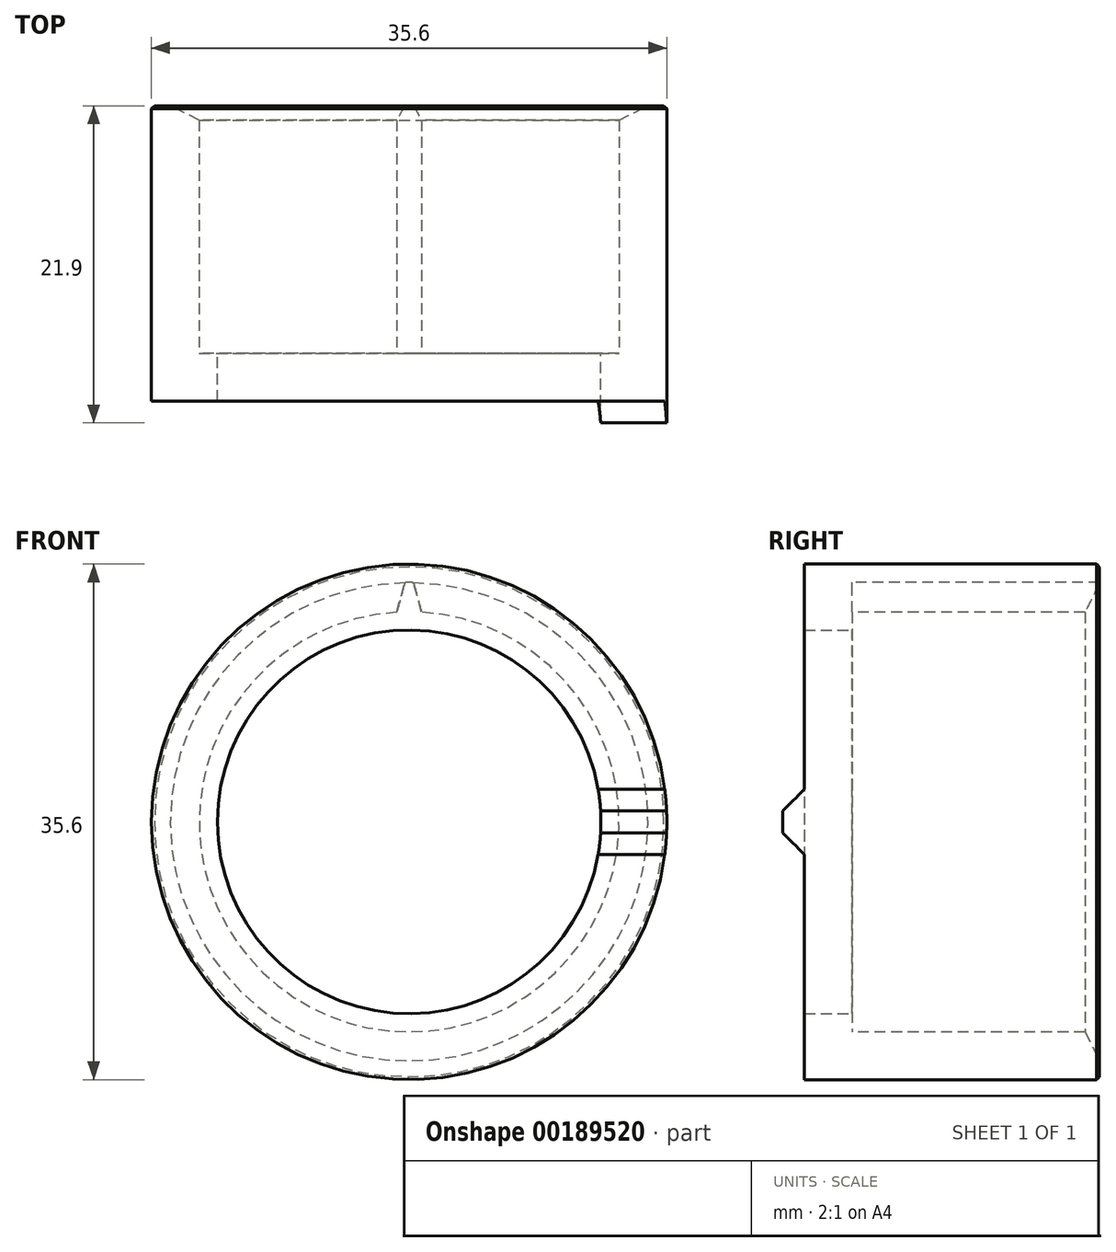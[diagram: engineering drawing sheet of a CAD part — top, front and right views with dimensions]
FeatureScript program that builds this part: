
annotation { "Feature Type Name" : "Feature", "Feature Type Description" : "" }
export const myFeature = defineFeature(function(context is Context, id is Id, definition is map)
    precondition{}
    {
        {
            var Q0;
            Q0=qCreatedBy(makeId("Front.planeOp"),FACE);
            var sketch = newSketch(context, id + "F0", { "sketchPlane" : qUnion([Q0])});
            skCircle(sketch, "E0", {"center": v(0, 0) * mm, "radius": 17.8 * mm});
            skCircle(sketch, "E1", {"center": v(0, 0) * mm, "radius": 14.5 * mm});
            skCircle(sketch, "E2", {"center": v(0, 0) * mm, "radius": 13.25 * mm});
            skSolve(sketch);
        }
        {
            var Q0;
            Q0=makeQuery(id+"F0.imprint","IMPRINT",FACE,{"disambiguationData":[TD([[makeQuery(id+"F0.imprint","IMPRINT",EDGE,{"derivedFrom":sQuery(id+"F0.wireOp",EDGE,"E0")}),1.0]])]});
            var Q1;
            Q1=makeQuery(id+"F0.imprint","IMPRINT",FACE,{"disambiguationData":[TD([[makeQuery(id+"F0.imprint","IMPRINT",EDGE,{"derivedFrom":sQuery(id+"F0.wireOp",EDGE,"E1")}),1.0]])]});
            extrude(context, id + "F1", {"entities" : qUnion([Q0, Q1]), "depth" : 3.3 * mm});
        }
        {
            var Q0;
            Q0=makeQuery(id+"F0.imprint","IMPRINT",FACE,{"disambiguationData":[TD([[makeQuery(id+"F0.imprint","IMPRINT",EDGE,{"derivedFrom":sQuery(id+"F0.wireOp",EDGE,"E0")}),1.0]])]});
            extrude(context, id + "F2", {"entities" : qUnion([Q0]), "operationType" : NewBodyOperationType.ADD, "oppositeDirection" : true, "depth" : (20.4 - 3.3) * mm});
        }
        {
            var Q0;
            Q0=makeQuery(id+"F2.opExtrude","CAP_EDGE",EDGE,{"disambiguationData":[OSD([sQuery(id+"F0.wireOp",EDGE,"E1")])],"isStart":false});
            chamfer(context, id + "F3", {"entities" : qUnion([Q0]), "chamferType" : ChamferType.TWO_OFFSETS, "width1" : 2 * mm, "oppositeDirection" : false, "width2" : 1 * mm, "tangentPropagation" : true});
        }
        {
            var Q0;
            Q0=qCreatedBy(makeId("Front.planeOp"),FACE);
            var sketch = newSketch(context, id + "F4", { "sketchPlane" : qUnion([Q0])});
            skLineSegment(sketch, "E3", {"start": v(0.38, -14.5) * mm, "end": v(1.1, -16.51) * mm});
            skArc(sketch, "E4", {"start": v(2.08, -14.35) * mm, "mid": v(2.45, -14.3) * mm, "end": v(2.82, -14.22) * mm});
            skArc(sketch, "E5", {"start": v(3.88, -16.09) * mm, "mid": v(4.17, -16.02) * mm, "end": v(4.46, -15.94) * mm});
            skLineSegment(sketch, "E6", {"start": v(-0.37, -14.5) * mm, "end": v(-1.1, -16.51) * mm});
            skLineSegment(sketch, "E7.1.0", {"start": v(2.82, -14.22) * mm, "end": v(3.88, -16.09) * mm});
            skLineSegment(sketch, "E7.1.1", {"start": v(2.08, -14.35) * mm, "end": v(1.7, -16.46) * mm});
            skLineSegment(sketch, "E7.2.0", {"start": v(5.18, -13.54) * mm, "end": v(6.55, -15.2) * mm});
            skLineSegment(sketch, "E7.2.1", {"start": v(4.48, -13.8) * mm, "end": v(4.46, -15.94) * mm});
            skLineSegment(sketch, "E7.3.0", {"start": v(7.4, -12.47) * mm, "end": v(9.02, -13.87) * mm});
            skLineSegment(sketch, "E7.3.1", {"start": v(6.74, -12.84) * mm, "end": v(7.08, -14.96) * mm});
            skLineSegment(sketch, "E7.4.0", {"start": v(9.4, -11.04) * mm, "end": v(11.24, -12.15) * mm});
            skLineSegment(sketch, "E7.4.1", {"start": v(8.81, -11.51) * mm, "end": v(9.51, -13.54) * mm});
            skLineSegment(sketch, "E7.5.0", {"start": v(11.13, -9.3) * mm, "end": v(13.13, -10.08) * mm});
            skLineSegment(sketch, "E7.5.1", {"start": v(10.63, -9.86) * mm, "end": v(11.66, -11.74) * mm});
            skLineSegment(sketch, "E7.6.0", {"start": v(12.54, -7.28) * mm, "end": v(14.64, -7.71) * mm});
            skLineSegment(sketch, "E7.6.1", {"start": v(12.15, -7.92) * mm, "end": v(13.48, -9.6) * mm});
            skLineSegment(sketch, "E7.7.0", {"start": v(13.59, -5.06) * mm, "end": v(15.74, -5.13) * mm});
            skLineSegment(sketch, "E7.7.1", {"start": v(13.31, -5.75) * mm, "end": v(14.9, -7.19) * mm});
            skLineSegment(sketch, "E7.8.0", {"start": v(14.25, -2.69) * mm, "end": v(16.38, -2.4) * mm});
            skLineSegment(sketch, "E7.8.1", {"start": v(14.1, -3.42) * mm, "end": v(15.9, -4.56) * mm});
            skLineSegment(sketch, "E7.9.0", {"start": v(14.5, -0.24) * mm, "end": v(16.54, 0.4) * mm});
            skLineSegment(sketch, "E7.9.1", {"start": v(14.47, -0.99) * mm, "end": v(16.45, -1.8) * mm});
            skLineSegment(sketch, "E7.10.0", {"start": v(14.33, 2.21) * mm, "end": v(16.24, 3.2) * mm});
            skLineSegment(sketch, "E7.10.1", {"start": v(14.43, 1.47) * mm, "end": v(16.52, 1) * mm});
            skLineSegment(sketch, "E7.11.0", {"start": v(13.75, 4.6) * mm, "end": v(15.46, 5.9) * mm});
            skLineSegment(sketch, "E7.11.1", {"start": v(13.97, 3.89) * mm, "end": v(16.11, 3.77) * mm});
            skLineSegment(sketch, "E7.12.0", {"start": v(12.77, 6.86) * mm, "end": v(14.25, 8.42) * mm});
            skLineSegment(sketch, "E7.12.1", {"start": v(13.11, 6.2) * mm, "end": v(15.24, 6.44) * mm});
            skLineSegment(sketch, "E7.13.0", {"start": v(11.43, 8.92) * mm, "end": v(12.62, 10.71) * mm});
            skLineSegment(sketch, "E7.13.1", {"start": v(11.88, 8.32) * mm, "end": v(13.94, 8.93) * mm});
            skLineSegment(sketch, "E7.14.0", {"start": v(9.76, 10.72) * mm, "end": v(10.62, 12.69) * mm});
            skLineSegment(sketch, "E7.14.1", {"start": v(10.3, 10.2) * mm, "end": v(12.23, 11.15) * mm});
            skLineSegment(sketch, "E7.15.0", {"start": v(7.8, 12.22) * mm, "end": v(8.33, 14.3) * mm});
            skLineSegment(sketch, "E7.15.1", {"start": v(8.43, 11.8) * mm, "end": v(10.17, 13.06) * mm});
            skLineSegment(sketch, "E7.16.0", {"start": v(5.63, 13.36) * mm, "end": v(5.8, 15.5) * mm});
            skLineSegment(sketch, "E7.16.1", {"start": v(6.31, 13.05) * mm, "end": v(7.81, 14.59) * mm});
            skLineSegment(sketch, "E7.17.0", {"start": v(3.29, 14.12) * mm, "end": v(3.09, 16.26) * mm});
            skLineSegment(sketch, "E7.17.1", {"start": v(4.02, 13.93) * mm, "end": v(5.23, 15.7) * mm});
            skLineSegment(sketch, "E7.18.0", {"start": v(0.86, 14.47) * mm, "end": v(0.3, 16.55) * mm});
            skLineSegment(sketch, "E7.18.1", {"start": v(1.6, 14.41) * mm, "end": v(2.5, 16.36) * mm});
            skLineSegment(sketch, "E7.19.0", {"start": v(-1.6, 14.41) * mm, "end": v(-2.5, 16.36) * mm});
            skLineSegment(sketch, "E7.19.1", {"start": v(-0.86, 14.47) * mm, "end": v(-0.3, 16.55) * mm});
            skLineSegment(sketch, "E7.20.0", {"start": v(-4.02, 13.93) * mm, "end": v(-5.23, 15.7) * mm});
            skLineSegment(sketch, "E7.20.1", {"start": v(-3.29, 14.12) * mm, "end": v(-3.09, 16.26) * mm});
            skLineSegment(sketch, "E7.21.0", {"start": v(-6.31, 13.05) * mm, "end": v(-7.81, 14.59) * mm});
            skLineSegment(sketch, "E7.21.1", {"start": v(-5.63, 13.36) * mm, "end": v(-5.8, 15.5) * mm});
            skLineSegment(sketch, "E7.22.0", {"start": v(-8.43, 11.8) * mm, "end": v(-10.17, 13.06) * mm});
            skLineSegment(sketch, "E7.22.1", {"start": v(-7.8, 12.22) * mm, "end": v(-8.33, 14.3) * mm});
            skLineSegment(sketch, "E7.23.0", {"start": v(-10.3, 10.2) * mm, "end": v(-12.23, 11.15) * mm});
            skLineSegment(sketch, "E7.23.1", {"start": v(-9.76, 10.72) * mm, "end": v(-10.62, 12.69) * mm});
            skLineSegment(sketch, "E7.24.0", {"start": v(-11.88, 8.32) * mm, "end": v(-13.94, 8.93) * mm});
            skLineSegment(sketch, "E7.24.1", {"start": v(-11.43, 8.92) * mm, "end": v(-12.62, 10.71) * mm});
            skLineSegment(sketch, "E7.25.0", {"start": v(-13.11, 6.2) * mm, "end": v(-15.24, 6.44) * mm});
            skLineSegment(sketch, "E7.25.1", {"start": v(-12.77, 6.86) * mm, "end": v(-14.25, 8.42) * mm});
            skLineSegment(sketch, "E7.26.0", {"start": v(-13.97, 3.89) * mm, "end": v(-16.11, 3.77) * mm});
            skLineSegment(sketch, "E7.26.1", {"start": v(-13.75, 4.6) * mm, "end": v(-15.46, 5.9) * mm});
            skLineSegment(sketch, "E7.27.0", {"start": v(-14.43, 1.47) * mm, "end": v(-16.52, 1) * mm});
            skLineSegment(sketch, "E7.27.1", {"start": v(-14.33, 2.21) * mm, "end": v(-16.24, 3.2) * mm});
            skLineSegment(sketch, "E7.28.0", {"start": v(-14.47, -0.99) * mm, "end": v(-16.45, -1.8) * mm});
            skLineSegment(sketch, "E7.28.1", {"start": v(-14.5, -0.24) * mm, "end": v(-16.54, 0.4) * mm});
            skLineSegment(sketch, "E7.29.0", {"start": v(-14.1, -3.42) * mm, "end": v(-15.9, -4.56) * mm});
            skLineSegment(sketch, "E7.29.1", {"start": v(-14.25, -2.69) * mm, "end": v(-16.38, -2.4) * mm});
            skLineSegment(sketch, "E7.30.0", {"start": v(-13.31, -5.75) * mm, "end": v(-14.9, -7.19) * mm});
            skLineSegment(sketch, "E7.30.1", {"start": v(-13.59, -5.06) * mm, "end": v(-15.74, -5.13) * mm});
            skLineSegment(sketch, "E7.31.0", {"start": v(-12.15, -7.92) * mm, "end": v(-13.48, -9.6) * mm});
            skLineSegment(sketch, "E7.31.1", {"start": v(-12.54, -7.28) * mm, "end": v(-14.64, -7.71) * mm});
            skLineSegment(sketch, "E7.32.0", {"start": v(-10.63, -9.86) * mm, "end": v(-11.66, -11.74) * mm});
            skLineSegment(sketch, "E7.32.1", {"start": v(-11.13, -9.3) * mm, "end": v(-13.13, -10.08) * mm});
            skLineSegment(sketch, "E7.33.0", {"start": v(-8.81, -11.51) * mm, "end": v(-9.51, -13.54) * mm});
            skLineSegment(sketch, "E7.33.1", {"start": v(-9.4, -11.04) * mm, "end": v(-11.24, -12.15) * mm});
            skLineSegment(sketch, "E7.34.0", {"start": v(-6.74, -12.84) * mm, "end": v(-7.08, -14.96) * mm});
            skLineSegment(sketch, "E7.34.1", {"start": v(-7.4, -12.47) * mm, "end": v(-9.02, -13.87) * mm});
            skLineSegment(sketch, "E7.35.0", {"start": v(-4.48, -13.8) * mm, "end": v(-4.46, -15.94) * mm});
            skLineSegment(sketch, "E7.35.1", {"start": v(-5.18, -13.54) * mm, "end": v(-6.55, -15.2) * mm});
            skLineSegment(sketch, "E7.36.0", {"start": v(-2.08, -14.35) * mm, "end": v(-1.7, -16.46) * mm});
            skLineSegment(sketch, "E7.36.1", {"start": v(-2.82, -14.22) * mm, "end": v(-3.88, -16.09) * mm});
            skArc(sketch, "E8.trimOffspring", {"start": v(1.1, -16.51) * mm, "mid": v(1.4, -16.5) * mm, "end": v(1.7, -16.46) * mm});
            skArc(sketch, "E9.trimOffspring", {"start": v(-0.37, -14.5) * mm, "mid": v(0, -14.5) * mm, "end": v(0.37, -14.5) * mm});
            skArc(sketch, "E10.trimOffspring", {"start": v(-1.7, -16.46) * mm, "mid": v(-1.4, -16.5) * mm, "end": v(-1.1, -16.51) * mm});
            skArc(sketch, "E11.trimOffspring", {"start": v(-2.82, -14.22) * mm, "mid": v(-2.45, -14.3) * mm, "end": v(-2.08, -14.35) * mm});
            skArc(sketch, "E12.trimOffspring", {"start": v(-4.46, -15.94) * mm, "mid": v(-4.17, -16.02) * mm, "end": v(-3.88, -16.09) * mm});
            skArc(sketch, "E13.trimOffspring", {"start": v(-5.18, -13.54) * mm, "mid": v(-4.83, -13.67) * mm, "end": v(-4.48, -13.8) * mm});
            skArc(sketch, "E14.trimOffspring", {"start": v(-7.08, -14.96) * mm, "mid": v(-6.82, -15.08) * mm, "end": v(-6.55, -15.2) * mm});
            skArc(sketch, "E15.trimOffspring", {"start": v(-7.4, -12.47) * mm, "mid": v(-7.07, -12.66) * mm, "end": v(-6.74, -12.84) * mm});
            skArc(sketch, "E16.trimOffspring", {"start": v(-9.51, -13.54) * mm, "mid": v(-9.27, -13.71) * mm, "end": v(-9.02, -13.87) * mm});
            skArc(sketch, "E17.trimOffspring", {"start": v(-9.4, -11.04) * mm, "mid": v(-9.1, -11.28) * mm, "end": v(-8.81, -11.51) * mm});
            skArc(sketch, "E18.trimOffspring", {"start": v(-11.66, -11.74) * mm, "mid": v(-11.45, -11.95) * mm, "end": v(-11.24, -12.15) * mm});
            skArc(sketch, "E19.trimOffspring", {"start": v(-11.13, -9.3) * mm, "mid": v(-10.88, -9.58) * mm, "end": v(-10.63, -9.86) * mm});
            skArc(sketch, "E20.trimOffspring", {"start": v(-13.48, -9.6) * mm, "mid": v(-13.3, -9.84) * mm, "end": v(-13.13, -10.08) * mm});
            skArc(sketch, "E21.trimOffspring", {"start": v(-12.54, -7.28) * mm, "mid": v(-12.35, -7.6) * mm, "end": v(-12.15, -7.92) * mm});
            skArc(sketch, "E22.trimOffspring", {"start": v(-14.9, -7.19) * mm, "mid": v(-14.78, -7.45) * mm, "end": v(-14.64, -7.71) * mm});
            skArc(sketch, "E23.trimOffspring", {"start": v(-13.59, -5.06) * mm, "mid": v(-13.45, -5.4) * mm, "end": v(-13.31, -5.75) * mm});
            skArc(sketch, "E24.trimOffspring", {"start": v(-15.9, -4.56) * mm, "mid": v(-15.82, -4.85) * mm, "end": v(-15.74, -5.13) * mm});
            skArc(sketch, "E25.trimOffspring", {"start": v(-14.25, -2.69) * mm, "mid": v(-14.17, -3.05) * mm, "end": v(-14.1, -3.42) * mm});
            skArc(sketch, "E26.trimOffspring", {"start": v(-16.45, -1.8) * mm, "mid": v(-16.42, -2.1) * mm, "end": v(-16.38, -2.4) * mm});
            skArc(sketch, "E27.trimOffspring", {"start": v(-14.5, -0.24) * mm, "mid": v(-14.49, -0.62) * mm, "end": v(-14.47, -0.99) * mm});
            skArc(sketch, "E28.trimOffspring", {"start": v(4.48, -13.8) * mm, "mid": v(4.83, -13.67) * mm, "end": v(5.18, -13.54) * mm});
            skArc(sketch, "E29.trimOffspring", {"start": v(6.55, -15.2) * mm, "mid": v(6.82, -15.08) * mm, "end": v(7.08, -14.96) * mm});
            skArc(sketch, "E30.trimOffspring", {"start": v(9.02, -13.87) * mm, "mid": v(9.27, -13.71) * mm, "end": v(9.51, -13.54) * mm});
            skArc(sketch, "E31.trimOffspring", {"start": v(11.24, -12.15) * mm, "mid": v(11.45, -11.95) * mm, "end": v(11.66, -11.74) * mm});
            skArc(sketch, "E32.trimOffspring", {"start": v(13.13, -10.08) * mm, "mid": v(13.3, -9.84) * mm, "end": v(13.48, -9.6) * mm});
            skArc(sketch, "E33.trimOffspring", {"start": v(8.81, -11.51) * mm, "mid": v(9.1, -11.28) * mm, "end": v(9.4, -11.04) * mm});
            skArc(sketch, "E34.trimOffspring", {"start": v(10.63, -9.86) * mm, "mid": v(10.88, -9.58) * mm, "end": v(11.13, -9.3) * mm});
            skArc(sketch, "E35.trimOffspring", {"start": v(6.74, -12.84) * mm, "mid": v(7.07, -12.66) * mm, "end": v(7.4, -12.47) * mm});
            skArc(sketch, "E36.trimOffspring", {"start": v(12.15, -7.92) * mm, "mid": v(12.35, -7.6) * mm, "end": v(12.54, -7.28) * mm});
            skArc(sketch, "E37.trimOffspring", {"start": v(13.31, -5.75) * mm, "mid": v(13.45, -5.4) * mm, "end": v(13.59, -5.06) * mm});
            skArc(sketch, "E38.trimOffspring", {"start": v(14.1, -3.42) * mm, "mid": v(14.17, -3.05) * mm, "end": v(14.25, -2.69) * mm});
            skArc(sketch, "E39.trimOffspring", {"start": v(14.47, -0.99) * mm, "mid": v(14.49, -0.62) * mm, "end": v(14.5, -0.24) * mm});
            skArc(sketch, "E40.trimOffspring", {"start": v(14.43, 1.47) * mm, "mid": v(14.38, 1.84) * mm, "end": v(14.33, 2.21) * mm});
            skArc(sketch, "E41.trimOffspring", {"start": v(14.64, -7.71) * mm, "mid": v(14.78, -7.45) * mm, "end": v(14.9, -7.19) * mm});
            skArc(sketch, "E42.trimOffspring", {"start": v(15.74, -5.13) * mm, "mid": v(15.82, -4.85) * mm, "end": v(15.9, -4.56) * mm});
            skArc(sketch, "E43.trimOffspring", {"start": v(16.38, -2.4) * mm, "mid": v(16.42, -2.1) * mm, "end": v(16.45, -1.8) * mm});
            skArc(sketch, "E44.trimOffspring", {"start": v(16.54, 0.4) * mm, "mid": v(16.54, 0.7) * mm, "end": v(16.52, 1) * mm});
            skArc(sketch, "E45.trimOffspring", {"start": v(16.24, 3.2) * mm, "mid": v(16.18, 3.49) * mm, "end": v(16.11, 3.77) * mm});
            skArc(sketch, "E46.trimOffspring", {"start": v(15.46, 5.9) * mm, "mid": v(15.36, 6.17) * mm, "end": v(15.24, 6.44) * mm});
            skArc(sketch, "E47.trimOffspring", {"start": v(14.25, 8.42) * mm, "mid": v(14.1, 8.68) * mm, "end": v(13.94, 8.93) * mm});
            skArc(sketch, "E48.trimOffspring", {"start": v(13.97, 3.89) * mm, "mid": v(13.86, 4.25) * mm, "end": v(13.75, 4.6) * mm});
            skArc(sketch, "E49.trimOffspring", {"start": v(13.11, 6.2) * mm, "mid": v(12.95, 6.53) * mm, "end": v(12.77, 6.86) * mm});
            skArc(sketch, "E50.trimOffspring", {"start": v(11.88, 8.32) * mm, "mid": v(11.66, 8.62) * mm, "end": v(11.43, 8.92) * mm});
            skArc(sketch, "E51.trimOffspring", {"start": v(-14.33, 2.21) * mm, "mid": v(-14.38, 1.84) * mm, "end": v(-14.43, 1.47) * mm});
            skArc(sketch, "E52.trimOffspring", {"start": v(-16.52, 1) * mm, "mid": v(-16.54, 0.7) * mm, "end": v(-16.54, 0.4) * mm});
            skArc(sketch, "E53.trimOffspring", {"start": v(-16.11, 3.77) * mm, "mid": v(-16.18, 3.49) * mm, "end": v(-16.24, 3.2) * mm});
            skArc(sketch, "E54.trimOffspring", {"start": v(-15.24, 6.44) * mm, "mid": v(-15.36, 6.17) * mm, "end": v(-15.46, 5.9) * mm});
            skArc(sketch, "E55.trimOffspring", {"start": v(-13.94, 8.93) * mm, "mid": v(-14.1, 8.68) * mm, "end": v(-14.25, 8.42) * mm});
            skArc(sketch, "E56.trimOffspring", {"start": v(-12.23, 11.15) * mm, "mid": v(-12.42, 10.93) * mm, "end": v(-12.62, 10.71) * mm});
            skArc(sketch, "E57.trimOffspring", {"start": v(-10.17, 13.06) * mm, "mid": v(-10.4, 12.88) * mm, "end": v(-10.62, 12.69) * mm});
            skArc(sketch, "E58.trimOffspring", {"start": v(-7.81, 14.59) * mm, "mid": v(-8.07, 14.45) * mm, "end": v(-8.33, 14.3) * mm});
            skArc(sketch, "E59.trimOffspring", {"start": v(-5.23, 15.7) * mm, "mid": v(-5.51, 15.6) * mm, "end": v(-5.8, 15.5) * mm});
            skArc(sketch, "E60.trimOffspring", {"start": v(-2.5, 16.36) * mm, "mid": v(-2.8, 16.31) * mm, "end": v(-3.09, 16.26) * mm});
            skArc(sketch, "E61.trimOffspring", {"start": v(3.09, 16.26) * mm, "mid": v(2.8, 16.31) * mm, "end": v(2.5, 16.36) * mm});
            skArc(sketch, "E62.trimOffspring", {"start": v(5.8, 15.5) * mm, "mid": v(5.51, 15.6) * mm, "end": v(5.23, 15.7) * mm});
            skArc(sketch, "E63.trimOffspring", {"start": v(8.33, 14.3) * mm, "mid": v(8.07, 14.45) * mm, "end": v(7.81, 14.59) * mm});
            skArc(sketch, "E64.trimOffspring", {"start": v(10.62, 12.69) * mm, "mid": v(10.4, 12.88) * mm, "end": v(10.17, 13.06) * mm});
            skArc(sketch, "E65.trimOffspring", {"start": v(12.62, 10.71) * mm, "mid": v(12.42, 10.93) * mm, "end": v(12.23, 11.15) * mm});
            skArc(sketch, "E66.trimOffspring", {"start": v(10.3, 10.2) * mm, "mid": v(10.03, 10.47) * mm, "end": v(9.76, 10.72) * mm});
            skArc(sketch, "E67.trimOffspring", {"start": v(8.43, 11.8) * mm, "mid": v(8.12, 12.01) * mm, "end": v(7.8, 12.22) * mm});
            skArc(sketch, "E68.trimOffspring", {"start": v(6.31, 13.05) * mm, "mid": v(5.97, 13.21) * mm, "end": v(5.63, 13.36) * mm});
            skArc(sketch, "E69.trimOffspring", {"start": v(4.02, 13.93) * mm, "mid": v(3.65, 14.03) * mm, "end": v(3.29, 14.12) * mm});
            skArc(sketch, "E70.trimOffspring", {"start": v(1.6, 14.41) * mm, "mid": v(1.23, 14.45) * mm, "end": v(0.86, 14.47) * mm});
            skArc(sketch, "E71.trimOffspring", {"start": v(-0.86, 14.47) * mm, "mid": v(-1.23, 14.45) * mm, "end": v(-1.6, 14.41) * mm});
            skArc(sketch, "E72.trimOffspring", {"start": v(-3.29, 14.12) * mm, "mid": v(-3.65, 14.03) * mm, "end": v(-4.02, 13.93) * mm});
            skArc(sketch, "E73.trimOffspring", {"start": v(-7.8, 12.22) * mm, "mid": v(-8.12, 12.01) * mm, "end": v(-8.43, 11.8) * mm});
            skArc(sketch, "E74.trimOffspring", {"start": v(-11.43, 8.92) * mm, "mid": v(-11.66, 8.62) * mm, "end": v(-11.88, 8.32) * mm});
            skArc(sketch, "E75.trimOffspring", {"start": v(-12.77, 6.86) * mm, "mid": v(-12.95, 6.53) * mm, "end": v(-13.11, 6.2) * mm});
            skArc(sketch, "E76.trimOffspring", {"start": v(-13.75, 4.6) * mm, "mid": v(-13.86, 4.25) * mm, "end": v(-13.97, 3.89) * mm});
            skCircle(sketch, "E77", {"center": v(0, 0) * mm, "radius": 13 * mm});
            skArc(sketch, "E78.trimOffspring", {"start": v(-9.76, 10.72) * mm, "mid": v(-10.03, 10.47) * mm, "end": v(-10.3, 10.2) * mm});
            skLineSegment(sketch, "E79", {"start": v(0.86, 14.47) * mm, "end": v(0.86, 14.47) * mm});
            skLineSegment(sketch, "E80", {"start": v(0.86, 14.47) * mm, "end": v(-0.86, 14.47) * mm});
            skLineSegment(sketch, "E81", {"start": v(-0.86, 14.47) * mm, "end": v(-0.86, 14.47) * mm});
            skLineSegment(sketch, "E82", {"start": v(0.3, 16.55) * mm, "end": v(0.3, 16.55) * mm});
            skLineSegment(sketch, "E83", {"start": v(0.3, 16.55) * mm, "end": v(-0.3, 16.55) * mm});
            skLineSegment(sketch, "E84", {"start": v(-0.3, 16.55) * mm, "end": v(-0.3, 16.55) * mm});
            skSolve(sketch);
        }
        {
            var Q0;
            Q0 = qSketchRegion(id + "F4", true);
            extrude(context, id + "F5", {"entities" : qUnion([Q0]), "operationType" : NewBodyOperationType.REMOVE, "oppositeDirection" : true, "depth" : 25 * mm});
        }
        {
            var Q0;
            Q0=makeQuery(id+"F5.boolean.opBoolean","COPY",EDGE,{"derivedFrom":makeQuery(id+"F5.opExtrude","SWEPT_EDGE",EDGE,{"disambiguationData":[OSD([sQuery(id+"F4.wireOp",EDGE,"E7.19.1"),sQuery(id+"F4.wireOp",EDGE,"E83")])]})});
            var Q1;
            Q1=makeQuery(id+"F5.boolean.opBoolean","COPY",EDGE,{"derivedFrom":makeQuery(id+"F5.opExtrude","SWEPT_EDGE",EDGE,{"disambiguationData":[OSD([sQuery(id+"F4.wireOp",EDGE,"E7.18.0"),sQuery(id+"F4.wireOp",EDGE,"E83")])]})});
            var Q2;
            Q2=makeQuery(id+"F5.boolean.opBoolean","COPY",EDGE,{"derivedFrom":makeQuery(id+"F5.opExtrude","SWEPT_EDGE",EDGE,{"disambiguationData":[OSD([sQuery(id+"F4.wireOp",EDGE,"E7.18.0"),sQuery(id+"F4.wireOp",EDGE,"E80")])]})});
            var Q3;
            Q3=makeQuery(id+"F5.boolean.opBoolean","COPY",EDGE,{"derivedFrom":makeQuery(id+"F5.opExtrude","SWEPT_EDGE",EDGE,{"disambiguationData":[OSD([sQuery(id+"F4.wireOp",EDGE,"E7.19.1"),sQuery(id+"F4.wireOp",EDGE,"E80")])]})});
            fillet(context, id + "F6", {"entities" : qUnion([Q0, Q1, Q2, Q3]), "radius" : 0.2 * mm, "tangentPropagation" : true, "allowEdgeOverflow" : false});
        }
        {
            var Q0;
            Q0=makeQuery(id+"F1.opExtrude","CAP_FACE",FACE,{"disambiguationData":[OSD([sQuery(id+"F0.wireOp",EDGE,"E0"),sQuery(id+"F0.wireOp",EDGE,"E2")])],"isStart":false});
            var sketch = newSketch(context, id + "F7", { "sketchPlane" : qUnion([Q0])});
            skLineSegment(sketch, "E85.bottom", {"start": v(9, 2.25) * mm, "end": v(23, 2.25) * mm});
            skLineSegment(sketch, "E85.top", {"start": v(9, -2.25) * mm, "end": v(23, -2.25) * mm});
            skLineSegment(sketch, "E85.left", {"start": v(9, 2.25) * mm, "end": v(9, -2.25) * mm});
            skLineSegment(sketch, "E85.right", {"start": v(23, 2.25) * mm, "end": v(23, -2.25) * mm});
            skCircle(sketch, "E86", {"center": v(0, 0) * mm, "radius": 13.25 * mm});
            skCircle(sketch, "E87", {"center": v(0, 0) * mm, "radius": 17.8 * mm});
            skSolve(sketch);
        }
        {
            var Q0;
            {var subQ0=sQuery(id+"F7.wireOp",EDGE,"E87");var subQ1=sQuery(id+"F7.wireOp",EDGE,"E85.bottom");var subQ2=makeQuery(id+"F7.imprint","INTERSECT",VERTEX,{"derivedFrom":[subQ1,subQ0]});Q0=makeQuery(id+"F7.imprint","IMPRINT",FACE,{"disambiguationData":[TD([[makeQuery(id+"F7.imprint","IMPRINT",EDGE,{"disambiguationData":[TD([[subQ2,1.0]])],"derivedFrom":subQ1}),-1.0]])]});}
            extrude(context, id + "F8", {"entities" : qUnion([Q0]), "operationType" : NewBodyOperationType.ADD, "depth" : 1.5 * mm});
        }
        {
            var Q0;
            Q0=makeQuery(id+"F8.opExtrude","CAP_EDGE",EDGE,{"disambiguationData":[OSD([sQuery(id+"F7.wireOp",EDGE,"E85.top")])],"isStart":false});
            var Q1;
            Q1=makeQuery(id+"F8.opExtrude","CAP_EDGE",EDGE,{"disambiguationData":[OSD([sQuery(id+"F7.wireOp",EDGE,"E85.bottom")])],"isStart":false});
            chamfer(context, id + "F9", {"entities" : qUnion([Q0, Q1]), "width" : 1.5 * mm, "tangentPropagation" : true});
        }
        {
            var Q0;
            Q0=makeQuery(id+"F2.opExtrude","CAP_EDGE",EDGE,{"disambiguationData":[OSD([sQuery(id+"F0.wireOp",EDGE,"E0")])],"isStart":false});
            chamfer(context, id + "F10", {"entities" : qUnion([Q0]), "width" : 0.2 * mm});
        }
    });
